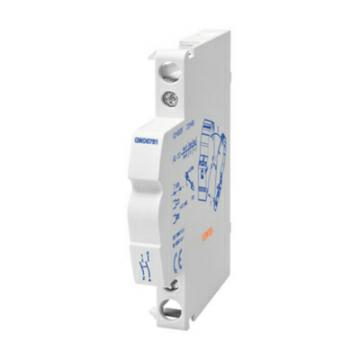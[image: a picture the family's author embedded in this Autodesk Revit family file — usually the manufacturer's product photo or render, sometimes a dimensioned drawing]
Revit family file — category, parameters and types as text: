
# Revit family: Power-ModularDevices-GEWISS-90AM-RELAY_RESIDUAL_CURRENT
name_source: partatom
category: Apparecchi elettrici
revit_build: Autodesk Revit 2016 (Build: 20161004_0715(x64)
units: mm (PartAtom-declared; Revit-internal decimal feet)

## family parameters
Condiviso = No
Host = Superficie
Mantenere orientamento annotazione = Sì
Numero OmniClass = 23.80.30.00
Punto di calcolo locali = Sì
Quota connettore circolare = Usa diametro
Taglio con vuoti quando caricato = No
Tipo di parte = Normale
Titolo OmniClass = Distribution Devices

## types (1)
- GW96331 - RESIDUAL CURRENT EARTH RELAY
    Assembly = DIN rail
    Catalogue = POWER
    Catalogue Range = 90 AM
    Descrizione = RESIDUAL CURRENT EARTH RELAY
    EAN code = 8011564177093
    Electrocod = 140
    Fin_INTERRUTTORE = <Per categoria>
    IDF = 7901679e-94c1-4048-a4bd-c1a92c425e58
    IDT = 8fce91a4-73eb-4b8b-b6af-6b6be4d5b2ce
    Immagine tipo = GW96331.jpg
    Installation = DIN rail
    Modello = GW96331
    No. Chorus modules = 3
    No. of modules EN 50022 = 3
    Numero poli = 1
    Potenza in Watt = 0 V
    Produttore = GEWISS S.p.A.
    Prospetto di default = 1219 mm
    Rated voltage = 230Vac
    Rated voltage (V) = 230 ac
    SEO = Relay
    TESTO ETICHETTA = A
    Technical sheet = https://www.gewiss.com
    Type = A
    Type: = Separate toroid
    URL = https://www.gewiss.com
    Version file RFA = 18.0
